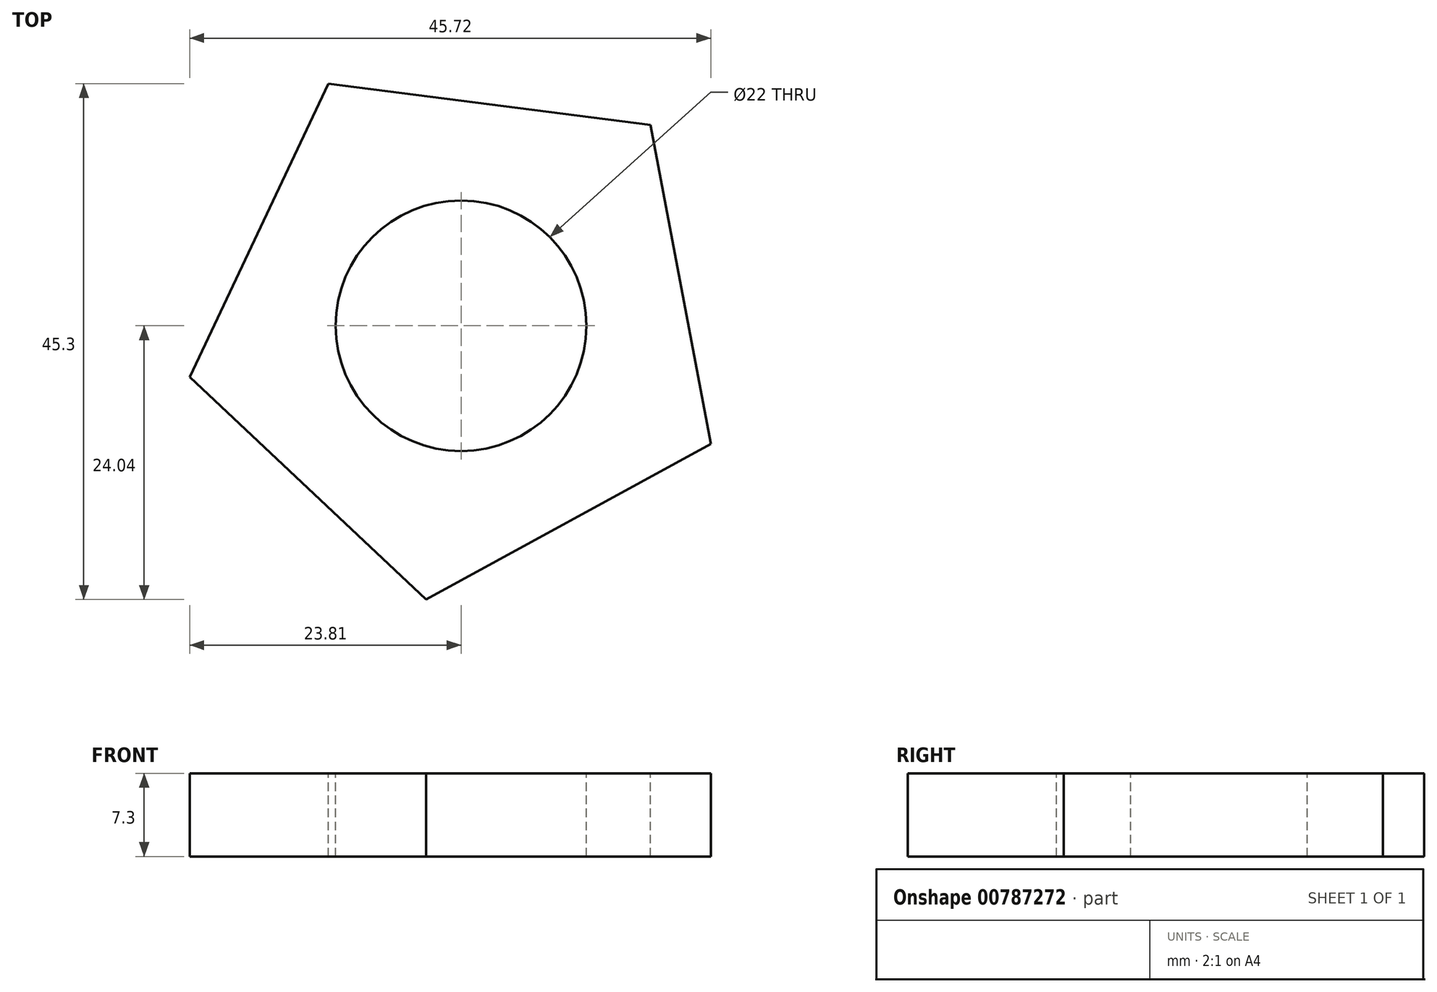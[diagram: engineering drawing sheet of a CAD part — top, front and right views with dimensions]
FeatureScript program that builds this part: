
annotation { "Feature Type Name" : "Feature", "Feature Type Description" : "" }
export const myFeature = defineFeature(function(context is Context, id is Id, definition is map)
    precondition{}
    {
        {
            var Q0;
            Q0=qCreatedBy(makeId("Top.planeOp"),FACE);
            var sketch = newSketch(context, id + "F0", { "sketchPlane" : qUnion([Q0])});
            skCircle(sketch, "E0", {"center": v(0, 0) * mm, "radius": 11 * mm});
            skSolve(sketch);
        }
        {
            var Q0;
            Q0=qCreatedBy(makeId("Top.planeOp"),FACE);
            var sketch = newSketch(context, id + "F1", { "sketchPlane" : qUnion([Q0])});
            skCircle(sketch, "E1.cCircle", {"center": v(0, 0) * mm, "radius": 19.6 * mm, "construction": true});
            skLineSegment(sketch, "E1.0", {"start": v(-3.08, -24.04) * mm, "end": v(-23.81, -4.5) * mm});
            skLineSegment(sketch, "E1.1", {"start": v(-23.81, -4.5) * mm, "end": v(-11.64, 21.26) * mm});
            skLineSegment(sketch, "E1.2", {"start": v(-11.64, 21.26) * mm, "end": v(16.62, 17.64) * mm});
            skLineSegment(sketch, "E1.3", {"start": v(16.62, 17.64) * mm, "end": v(21.9, -10.36) * mm});
            skLineSegment(sketch, "E1.4", {"start": v(21.9, -10.36) * mm, "end": v(-3.08, -24.04) * mm});
            skPoint(sketch, "E1.0.midPoint", {"position": v(-13.45, -14.27) * mm});
            skSolve(sketch);
        }
        {
            var Q0;
            Q0=makeQuery(id+"F1.imprint","IMPRINT",FACE,{"disambiguationData":[TD([[makeQuery(id+"F1.imprint","IMPRINT",EDGE,{"derivedFrom":sQuery(id+"F1.wireOp",EDGE,"E1.0")}),-1.0]])]});
            extrude(context, id + "F2", {"entities" : qUnion([Q0]), "oppositeDirection" : true, "depth" : 7 * mm, "offsetDistance" : 25 * mm});
        }
        {
            var Q0;
            Q0=makeQuery(id+"F2.opExtrude","CAP_FACE",FACE,{"disambiguationData":[OSD([sQuery(id+"F1.wireOp",EDGE,"E1.0"),sQuery(id+"F1.wireOp",EDGE,"E1.1"),sQuery(id+"F1.wireOp",EDGE,"E1.2"),sQuery(id+"F1.wireOp",EDGE,"E1.3"),sQuery(id+"F1.wireOp",EDGE,"E1.4")])],"isStart":false});
            extrude(context, id + "F3", {"entities" : qUnion([Q0]), "operationType" : NewBodyOperationType.ADD, "depth" : 2.6 * mm, "offsetDistance" : 25 * mm});
        }
        {
            var Q0;
            Q0=makeQuery(id+"F0.imprint","IMPRINT",FACE,{"disambiguationData":[TD([[makeQuery(id+"F0.imprint","IMPRINT",EDGE,{"derivedFrom":sQuery(id+"F0.wireOp",EDGE,"E0")}),1.0]])]});
            var Q1;
            Q1=sQuery(id+"F0.wireOp",EDGE,"E0");
            extrude(context, id + "F4", {"entities" : qUnion([Q0]), "operationType" : NewBodyOperationType.REMOVE, "surfaceEntities" : qUnion([Q1]), "oppositeDirection" : true, "depth" : 25 * mm, "offsetDistance" : 25 * mm});
        }
        {
            var Q0;
            Q0=makeQuery(id+"F3.opExtrude","CAP_FACE",FACE,{"disambiguationData":[OSD([sQuery(id+"F1.wireOp",EDGE,"E1.0"),sQuery(id+"F1.wireOp",EDGE,"E1.1"),sQuery(id+"F1.wireOp",EDGE,"E1.2"),sQuery(id+"F1.wireOp",EDGE,"E1.3"),sQuery(id+"F1.wireOp",EDGE,"E1.4")])],"isStart":false});
            extrude(context, id + "F5", {"entities" : qUnion([Q0]), "operationType" : NewBodyOperationType.REMOVE, "oppositeDirection" : true, "depth" : 2.3 * mm, "offsetDistance" : 25 * mm});
        }
    });
